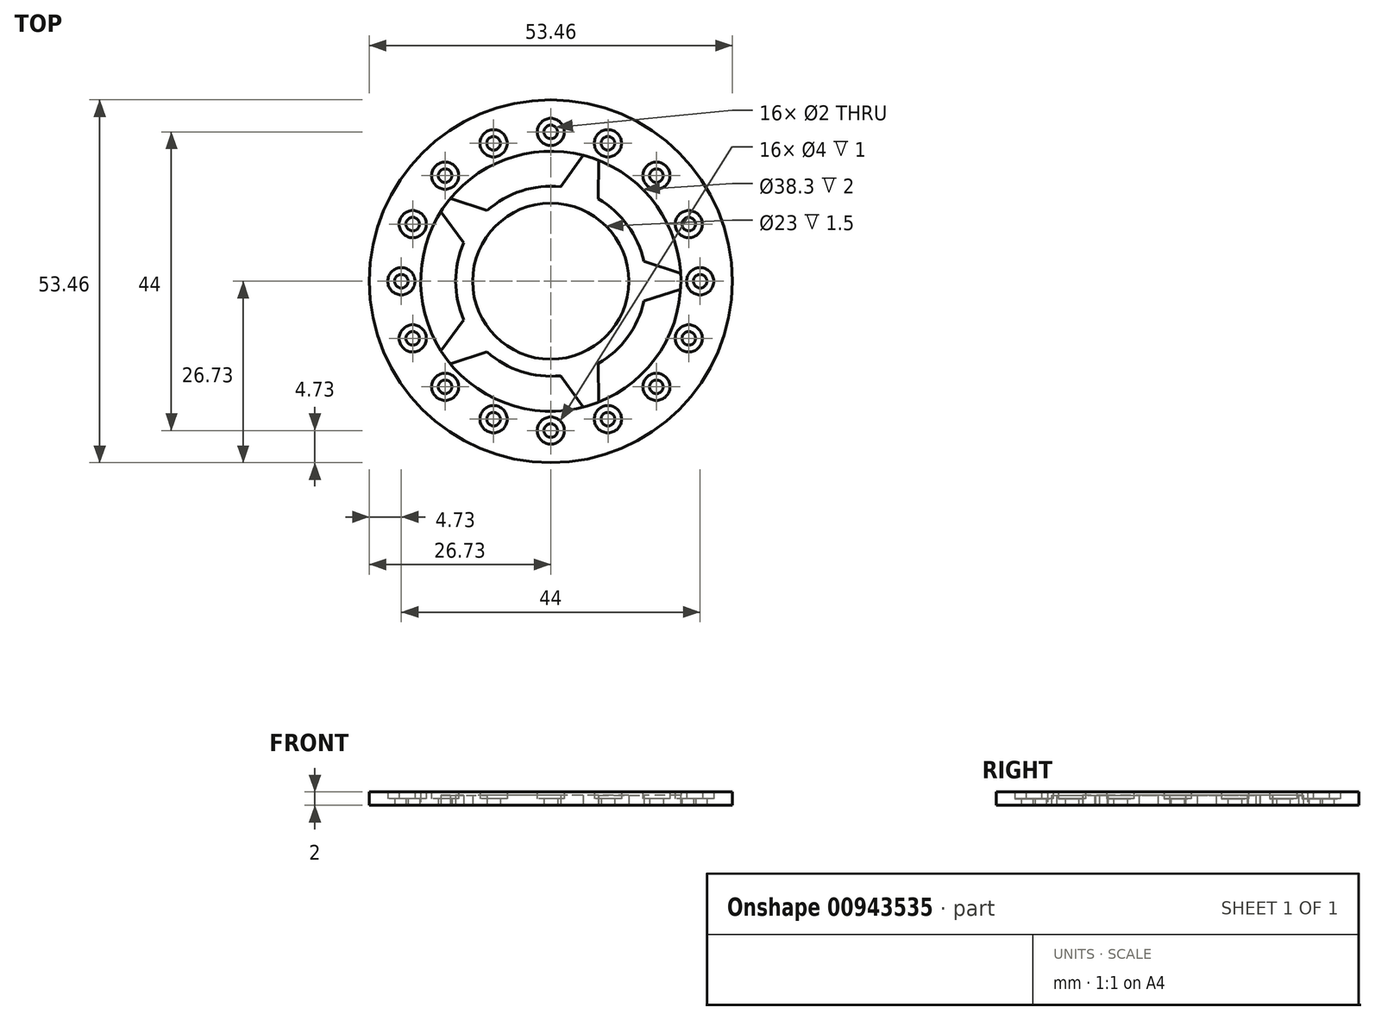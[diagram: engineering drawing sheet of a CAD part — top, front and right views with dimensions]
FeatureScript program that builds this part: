
annotation { "Feature Type Name" : "Feature", "Feature Type Description" : "" }
export const myFeature = defineFeature(function(context is Context, id is Id, definition is map)
    precondition{}
    {
        {
            var Q0;
            Q0=qCreatedBy(makeId("Top.planeOp"),FACE);
            var sketch = newSketch(context, id + "F0", { "sketchPlane" : qUnion([Q0])});
            skArc(sketch, "E0", {"start": v(-16.16, 10.27) * mm, "mid": v(-19.15, 0) * mm, "end": v(-16.16, -10.27) * mm});
            skCircle(sketch, "E1", {"center": v(22, 0) * mm, "radius": 1 * mm});
            skCircle(sketch, "E2", {"center": v(0, 0) * mm, "radius": 26.73 * mm});
            skCircle(sketch, "E3", {"center": v(0, 0) * mm, "radius": 11.5 * mm});
            skArc(sketch, "E4.0", {"start": v(-12.8, 5.7) * mm, "mid": v(-14, 0) * mm, "end": v(-12.8, -5.7) * mm});
            skLineSegment(sketch, "E5", {"start": v(19.11, 1.2) * mm, "end": v(13.7, 2.91) * mm});
            skLineSegment(sketch, "E6.MirrorCS", {"start": v(19.11, -1.2) * mm, "end": v(13.7, -2.91) * mm});
            skCircle(sketch, "E7.1.0", {"center": v(20.33, 8.42) * mm, "radius": 1 * mm});
            skCircle(sketch, "E7.2.0", {"center": v(15.56, 15.56) * mm, "radius": 1 * mm});
            skCircle(sketch, "E7.3.0", {"center": v(8.42, 20.33) * mm, "radius": 1 * mm});
            skCircle(sketch, "E7.4.0", {"center": v(0, 22) * mm, "radius": 1 * mm});
            skCircle(sketch, "E7.5.0", {"center": v(-8.42, 20.33) * mm, "radius": 1 * mm});
            skCircle(sketch, "E7.6.0", {"center": v(-15.56, 15.56) * mm, "radius": 1 * mm});
            skCircle(sketch, "E7.7.0", {"center": v(-20.33, 8.42) * mm, "radius": 1 * mm});
            skCircle(sketch, "E7.8.0", {"center": v(-22, 0) * mm, "radius": 1 * mm});
            skCircle(sketch, "E7.9.0", {"center": v(-20.33, -8.42) * mm, "radius": 1 * mm});
            skCircle(sketch, "E7.10.0", {"center": v(-15.56, -15.56) * mm, "radius": 1 * mm});
            skCircle(sketch, "E7.11.0", {"center": v(-8.42, -20.33) * mm, "radius": 1 * mm});
            skCircle(sketch, "E7.12.0", {"center": v(0, -22) * mm, "radius": 1 * mm});
            skCircle(sketch, "E7.13.0", {"center": v(8.42, -20.33) * mm, "radius": 1 * mm});
            skCircle(sketch, "E7.14.0", {"center": v(15.56, -15.56) * mm, "radius": 1 * mm});
            skCircle(sketch, "E7.15.0", {"center": v(20.33, -8.42) * mm, "radius": 1 * mm});
            skLineSegment(sketch, "E8.1.0", {"start": v(4.77, 18.55) * mm, "end": v(1.46, 13.92) * mm});
            skLineSegment(sketch, "E8.1.1", {"start": v(7.04, 17.8) * mm, "end": v(7, 12.12) * mm});
            skLineSegment(sketch, "E8.2.0", {"start": v(-16.16, 10.27) * mm, "end": v(-12.8, 5.7) * mm});
            skLineSegment(sketch, "E8.2.1", {"start": v(-14.76, 12.2) * mm, "end": v(-9.37, 10.4) * mm});
            skLineSegment(sketch, "E8.3.0", {"start": v(-14.76, -12.2) * mm, "end": v(-9.37, -10.4) * mm});
            skLineSegment(sketch, "E8.3.1", {"start": v(-16.16, -10.27) * mm, "end": v(-12.8, -5.7) * mm});
            skLineSegment(sketch, "E8.4.0", {"start": v(7.04, -17.8) * mm, "end": v(7, -12.12) * mm});
            skLineSegment(sketch, "E8.4.1", {"start": v(4.77, -18.55) * mm, "end": v(1.46, -13.92) * mm});
            skArc(sketch, "E9.trimOffspring", {"start": v(-9.37, -10.4) * mm, "mid": v(-4.33, -13.31) * mm, "end": v(1.46, -13.92) * mm});
            skArc(sketch, "E10.trimOffspring", {"start": v(-14.76, -12.2) * mm, "mid": v(-5.92, -18.21) * mm, "end": v(4.77, -18.55) * mm});
            skArc(sketch, "E11.trimOffspring", {"start": v(7.04, -17.8) * mm, "mid": v(15.5, -11.26) * mm, "end": v(19.11, -1.2) * mm});
            skArc(sketch, "E12.trimOffspring", {"start": v(7, -12.12) * mm, "mid": v(11.33, -8.23) * mm, "end": v(13.7, -2.91) * mm});
            skArc(sketch, "E13.trimOffspring", {"start": v(19.11, 1.2) * mm, "mid": v(15.5, 11.26) * mm, "end": v(7.04, 17.8) * mm});
            skArc(sketch, "E14.trimOffspring", {"start": v(13.7, 2.91) * mm, "mid": v(4.33, 13.31) * mm, "end": v(-9.37, 10.4) * mm});
            skArc(sketch, "E15.trimOffspring", {"start": v(4.77, 18.55) * mm, "mid": v(-5.92, 18.21) * mm, "end": v(-14.76, 12.2) * mm});
            skSolve(sketch);
        }
        {
            var Q0;
            Q0 = qSketchRegion(id + "F0", true);
            extrude(context, id + "F1", {"entities" : qUnion([Q0]), "depth" : 1.5 * mm, "offsetDistance" : 25 * mm});
        }
        {
            var Q0;
            Q0=makeQuery(id+"F1.opExtrude","CAP_FACE",FACE,{"disambiguationData":[OSD([sQuery(id+"F0.wireOp",EDGE,"E0"),sQuery(id+"F0.wireOp",EDGE,"E1"),sQuery(id+"F0.wireOp",EDGE,"E2"),sQuery(id+"F0.wireOp",EDGE,"E3"),sQuery(id+"F0.wireOp",EDGE,"E4.0"),sQuery(id+"F0.wireOp",EDGE,"E5"),sQuery(id+"F0.wireOp",EDGE,"E6.MirrorCS"),sQuery(id+"F0.wireOp",EDGE,"E7.1.0"),sQuery(id+"F0.wireOp",EDGE,"E7.2.0"),sQuery(id+"F0.wireOp",EDGE,"E7.3.0"),sQuery(id+"F0.wireOp",EDGE,"E7.4.0"),sQuery(id+"F0.wireOp",EDGE,"E7.5.0"),sQuery(id+"F0.wireOp",EDGE,"E7.6.0"),sQuery(id+"F0.wireOp",EDGE,"E7.7.0"),sQuery(id+"F0.wireOp",EDGE,"E7.8.0"),sQuery(id+"F0.wireOp",EDGE,"E7.9.0"),sQuery(id+"F0.wireOp",EDGE,"E7.10.0"),sQuery(id+"F0.wireOp",EDGE,"E7.11.0"),sQuery(id+"F0.wireOp",EDGE,"E7.12.0"),sQuery(id+"F0.wireOp",EDGE,"E7.13.0"),sQuery(id+"F0.wireOp",EDGE,"E7.14.0"),sQuery(id+"F0.wireOp",EDGE,"E7.15.0"),sQuery(id+"F0.wireOp",EDGE,"E8.1.0"),sQuery(id+"F0.wireOp",EDGE,"E8.1.1"),sQuery(id+"F0.wireOp",EDGE,"E8.2.0"),sQuery(id+"F0.wireOp",EDGE,"E8.2.1"),sQuery(id+"F0.wireOp",EDGE,"E8.3.0"),sQuery(id+"F0.wireOp",EDGE,"E8.3.1"),sQuery(id+"F0.wireOp",EDGE,"E8.4.0"),sQuery(id+"F0.wireOp",EDGE,"E8.4.1"),sQuery(id+"F0.wireOp",EDGE,"E9.trimOffspring"),sQuery(id+"F0.wireOp",EDGE,"E10.trimOffspring"),sQuery(id+"F0.wireOp",EDGE,"E11.trimOffspring"),sQuery(id+"F0.wireOp",EDGE,"E12.trimOffspring"),sQuery(id+"F0.wireOp",EDGE,"E13.trimOffspring"),sQuery(id+"F0.wireOp",EDGE,"E14.trimOffspring"),sQuery(id+"F0.wireOp",EDGE,"E15.trimOffspring")])],"isStart":false});
            var sketch = newSketch(context, id + "F2", { "sketchPlane" : qUnion([Q0])});
            skCircle(sketch, "E16.0", {"center": v(22, 0) * mm, "radius": 2 * mm});
            skCircle(sketch, "E17.1.0", {"center": v(20.33, 8.42) * mm, "radius": 2 * mm});
            skCircle(sketch, "E17.2.0", {"center": v(15.56, 15.56) * mm, "radius": 2 * mm});
            skCircle(sketch, "E17.3.0", {"center": v(8.42, 20.33) * mm, "radius": 2 * mm});
            skCircle(sketch, "E17.4.0", {"center": v(0, 22) * mm, "radius": 2 * mm});
            skCircle(sketch, "E17.5.0", {"center": v(-8.42, 20.33) * mm, "radius": 2 * mm});
            skCircle(sketch, "E17.6.0", {"center": v(-15.56, 15.56) * mm, "radius": 2 * mm});
            skCircle(sketch, "E17.7.0", {"center": v(-20.33, 8.42) * mm, "radius": 2 * mm});
            skCircle(sketch, "E17.8.0", {"center": v(-22, 0) * mm, "radius": 2 * mm});
            skCircle(sketch, "E17.9.0", {"center": v(-20.33, -8.42) * mm, "radius": 2 * mm});
            skCircle(sketch, "E17.10.0", {"center": v(-15.56, -15.56) * mm, "radius": 2 * mm});
            skCircle(sketch, "E17.11.0", {"center": v(-8.42, -20.33) * mm, "radius": 2 * mm});
            skCircle(sketch, "E17.12.0", {"center": v(0, -22) * mm, "radius": 2 * mm});
            skCircle(sketch, "E17.13.0", {"center": v(8.42, -20.33) * mm, "radius": 2 * mm});
            skCircle(sketch, "E17.14.0", {"center": v(15.56, -15.56) * mm, "radius": 2 * mm});
            skCircle(sketch, "E17.15.0", {"center": v(20.33, -8.42) * mm, "radius": 2 * mm});
            skPoint(sketch, "E17.center", {"position": v(0, 0) * mm});
            skCircle(sketch, "E18", {"center": v(0, 0) * mm, "radius": 19.15 * mm});
            skCircle(sketch, "E19.0", {"center": v(0, 0) * mm, "radius": 26.73 * mm});
            skSolve(sketch);
        }
        {
            var Q0;
            Q0 = qSketchRegion(id + "F2", true);
            extrude(context, id + "F3", {"entities" : qUnion([Q0]), "operationType" : NewBodyOperationType.ADD, "depth" : .5 * mm, "offsetDistance" : 25 * mm});
        }
        {
            var Q0;
            Q0=makeQuery(id+"F3.opExtrude","CAP_FACE",FACE,{"disambiguationData":[OSD([sQuery(id+"F2.wireOp",EDGE,"E16.0"),sQuery(id+"F2.wireOp",EDGE,"E17.1.0"),sQuery(id+"F2.wireOp",EDGE,"E17.2.0"),sQuery(id+"F2.wireOp",EDGE,"E17.3.0"),sQuery(id+"F2.wireOp",EDGE,"E17.4.0"),sQuery(id+"F2.wireOp",EDGE,"E17.5.0"),sQuery(id+"F2.wireOp",EDGE,"E17.6.0"),sQuery(id+"F2.wireOp",EDGE,"E17.7.0"),sQuery(id+"F2.wireOp",EDGE,"E17.8.0"),sQuery(id+"F2.wireOp",EDGE,"E17.9.0"),sQuery(id+"F2.wireOp",EDGE,"E17.10.0"),sQuery(id+"F2.wireOp",EDGE,"E17.11.0"),sQuery(id+"F2.wireOp",EDGE,"E17.12.0"),sQuery(id+"F2.wireOp",EDGE,"E17.13.0"),sQuery(id+"F2.wireOp",EDGE,"E17.14.0"),sQuery(id+"F2.wireOp",EDGE,"E17.15.0"),sQuery(id+"F2.wireOp",EDGE,"E18"),sQuery(id+"F2.wireOp",EDGE,"E19.0")])],"isStart":false});
            var sketch = newSketch(context, id + "F4", { "sketchPlane" : qUnion([Q0])});
            skCircle(sketch, "E20.0", {"center": v(-22, 0) * mm, "radius": 2 * mm});
            skCircle(sketch, "E20.1", {"center": v(-20.33, 8.42) * mm, "radius": 2 * mm});
            skCircle(sketch, "E20.2", {"center": v(-15.56, 15.56) * mm, "radius": 2 * mm});
            skCircle(sketch, "E20.3", {"center": v(-8.42, 20.33) * mm, "radius": 2 * mm});
            skCircle(sketch, "E20.4", {"center": v(0, 22) * mm, "radius": 2 * mm});
            skCircle(sketch, "E20.5", {"center": v(8.42, 20.33) * mm, "radius": 2 * mm});
            skCircle(sketch, "E20.6", {"center": v(15.56, 15.56) * mm, "radius": 2 * mm});
            skCircle(sketch, "E20.7", {"center": v(20.33, 8.42) * mm, "radius": 2 * mm});
            skCircle(sketch, "E20.8", {"center": v(22, 0) * mm, "radius": 2 * mm});
            skCircle(sketch, "E20.9", {"center": v(20.33, -8.42) * mm, "radius": 2 * mm});
            skCircle(sketch, "E20.10", {"center": v(15.56, -15.56) * mm, "radius": 2 * mm});
            skCircle(sketch, "E20.11", {"center": v(8.42, -20.33) * mm, "radius": 2 * mm});
            skCircle(sketch, "E20.12", {"center": v(0, -22) * mm, "radius": 2 * mm});
            skCircle(sketch, "E20.13", {"center": v(-8.42, -20.33) * mm, "radius": 2 * mm});
            skCircle(sketch, "E20.14", {"center": v(-15.56, -15.56) * mm, "radius": 2 * mm});
            skCircle(sketch, "E20.15", {"center": v(-20.33, -8.42) * mm, "radius": 2 * mm});
            skSolve(sketch);
        }
        {
            var Q0;
            Q0 = qSketchRegion(id + "F4", true);
            extrude(context, id + "F5", {"entities" : qUnion([Q0]), "operationType" : NewBodyOperationType.REMOVE, "oppositeDirection" : true, "depth" : 1 * mm, "offsetDistance" : 25 * mm});
        }
    });
